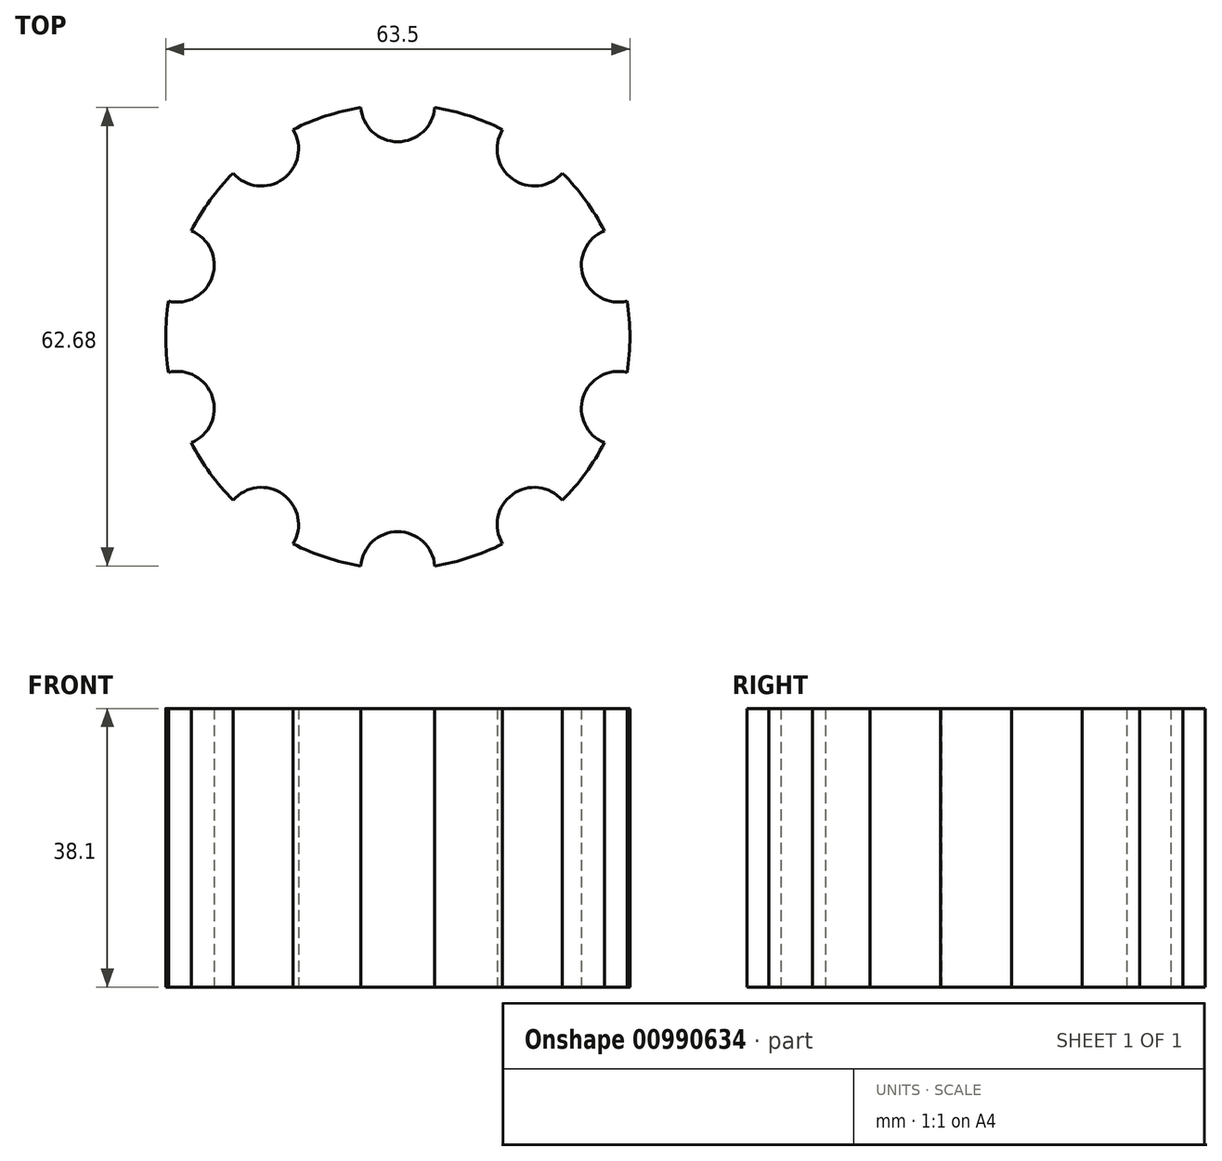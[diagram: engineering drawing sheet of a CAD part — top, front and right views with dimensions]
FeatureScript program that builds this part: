
annotation { "Feature Type Name" : "Feature", "Feature Type Description" : "" }
export const myFeature = defineFeature(function(context is Context, id is Id, definition is map)
    precondition{}
    {
        {
            var Q0;
            Q0=qCreatedBy(makeId("Top.planeOp"),FACE);
            var sketch = newSketch(context, id + "F0", { "sketchPlane" : qUnion([Q0])});
            skCircle(sketch, "E0", {"center": v(0, 0) * mm, "radius": 31.75 * mm});
            skSolve(sketch);
        }
        {
            var Q0;
            Q0=makeQuery(id+"F0.imprint","IMPRINT",FACE,{"disambiguationData":[TD([[makeQuery(id+"F0.imprint","IMPRINT",EDGE,{"derivedFrom":sQuery(id+"F0.wireOp",EDGE,"E0")}),1.0]])]});
            extrude(context, id + "F1", {"entities" : qUnion([Q0]), "depth" : 38.1 * mm});
        }
        {
            var Q0;
            Q0=qCreatedBy(makeId("Top.planeOp"),FACE);
            var sketch = newSketch(context, id + "F2", { "sketchPlane" : qUnion([Q0])});
            skCircle(sketch, "E1", {"center": v(0, 31.75) * mm, "radius": 5.08 * mm});
            skCircle(sketch, "E2.1.0", {"center": v(-18.66, 25.69) * mm, "radius": 5.08 * mm});
            skCircle(sketch, "E2.2.0", {"center": v(-30.2, 9.81) * mm, "radius": 5.08 * mm});
            skCircle(sketch, "E2.3.0", {"center": v(-30.2, -9.81) * mm, "radius": 5.08 * mm});
            skCircle(sketch, "E2.4.0", {"center": v(-18.66, -25.69) * mm, "radius": 5.08 * mm});
            skCircle(sketch, "E2.5.0", {"center": v(0, -31.75) * mm, "radius": 5.08 * mm});
            skCircle(sketch, "E2.6.0", {"center": v(18.66, -25.69) * mm, "radius": 5.08 * mm});
            skCircle(sketch, "E2.7.0", {"center": v(30.2, -9.81) * mm, "radius": 5.08 * mm});
            skCircle(sketch, "E2.8.0", {"center": v(30.2, 9.81) * mm, "radius": 5.08 * mm});
            skCircle(sketch, "E2.9.0", {"center": v(18.66, 25.69) * mm, "radius": 5.08 * mm});
            skPoint(sketch, "E2.center", {"position": v(0, 0) * mm});
            skSolve(sketch);
        }
        {
            var Q0;
            Q0=qSketchRegion(id+"F2",true);
            extrude(context, id + "F3", {"entities" : qUnion([Q0]), "depth" : 50.8 * mm});
        }
        {
            var Q0;
            Q0=makeQuery(id+"F3.opExtrude","SWEPT_BODY",BODY,{"disambiguationData":[OSD([sQuery(id+"F2.wireOp",EDGE,"E2.2.0")])]});
            var Q1;
            Q1=makeQuery(id+"F3.opExtrude","SWEPT_BODY",BODY,{"disambiguationData":[OSD([sQuery(id+"F2.wireOp",EDGE,"E2.1.0")])]});
            var Q2;
            Q2=makeQuery(id+"F3.opExtrude","SWEPT_BODY",BODY,{"disambiguationData":[OSD([sQuery(id+"F2.wireOp",EDGE,"E1")])]});
            var Q3;
            Q3=makeQuery(id+"F3.opExtrude","SWEPT_BODY",BODY,{"disambiguationData":[OSD([sQuery(id+"F2.wireOp",EDGE,"E2.8.0")])]});
            var Q4;
            Q4=makeQuery(id+"F3.opExtrude","SWEPT_BODY",BODY,{"disambiguationData":[OSD([sQuery(id+"F2.wireOp",EDGE,"E2.6.0")])]});
            var Q5;
            Q5=makeQuery(id+"F3.opExtrude","SWEPT_BODY",BODY,{"disambiguationData":[OSD([sQuery(id+"F2.wireOp",EDGE,"E2.5.0")])]});
            var Q6;
            Q6=makeQuery(id+"F3.opExtrude","SWEPT_BODY",BODY,{"disambiguationData":[OSD([sQuery(id+"F2.wireOp",EDGE,"E2.4.0")])]});
            var Q7;
            Q7=makeQuery(id+"F3.opExtrude","SWEPT_BODY",BODY,{"disambiguationData":[OSD([sQuery(id+"F2.wireOp",EDGE,"E2.3.0")])]});
            var Q8;
            Q8=makeQuery(id+"F3.opExtrude","SWEPT_BODY",BODY,{"disambiguationData":[OSD([sQuery(id+"F2.wireOp",EDGE,"E2.9.0")])]});
            var Q9;
            Q9=makeQuery(id+"F3.opExtrude","SWEPT_BODY",BODY,{"disambiguationData":[OSD([sQuery(id+"F2.wireOp",EDGE,"E2.7.0")])]});
            var Q10;
            Q10=makeQuery(id+"F1.opExtrude","SWEPT_BODY",BODY,{"disambiguationData":[OSD([sQuery(id+"F0.wireOp",EDGE,"E0")])]});
            booleanBodies(context, id + "F4", {"operationType" : BooleanOperationType.SUBTRACTION, "tools" : qUnion([Q0, Q1, Q2, Q3, Q4, Q5, Q6, Q7, Q8, Q9]), "targets" : qUnion([Q10])});
        }
    });
